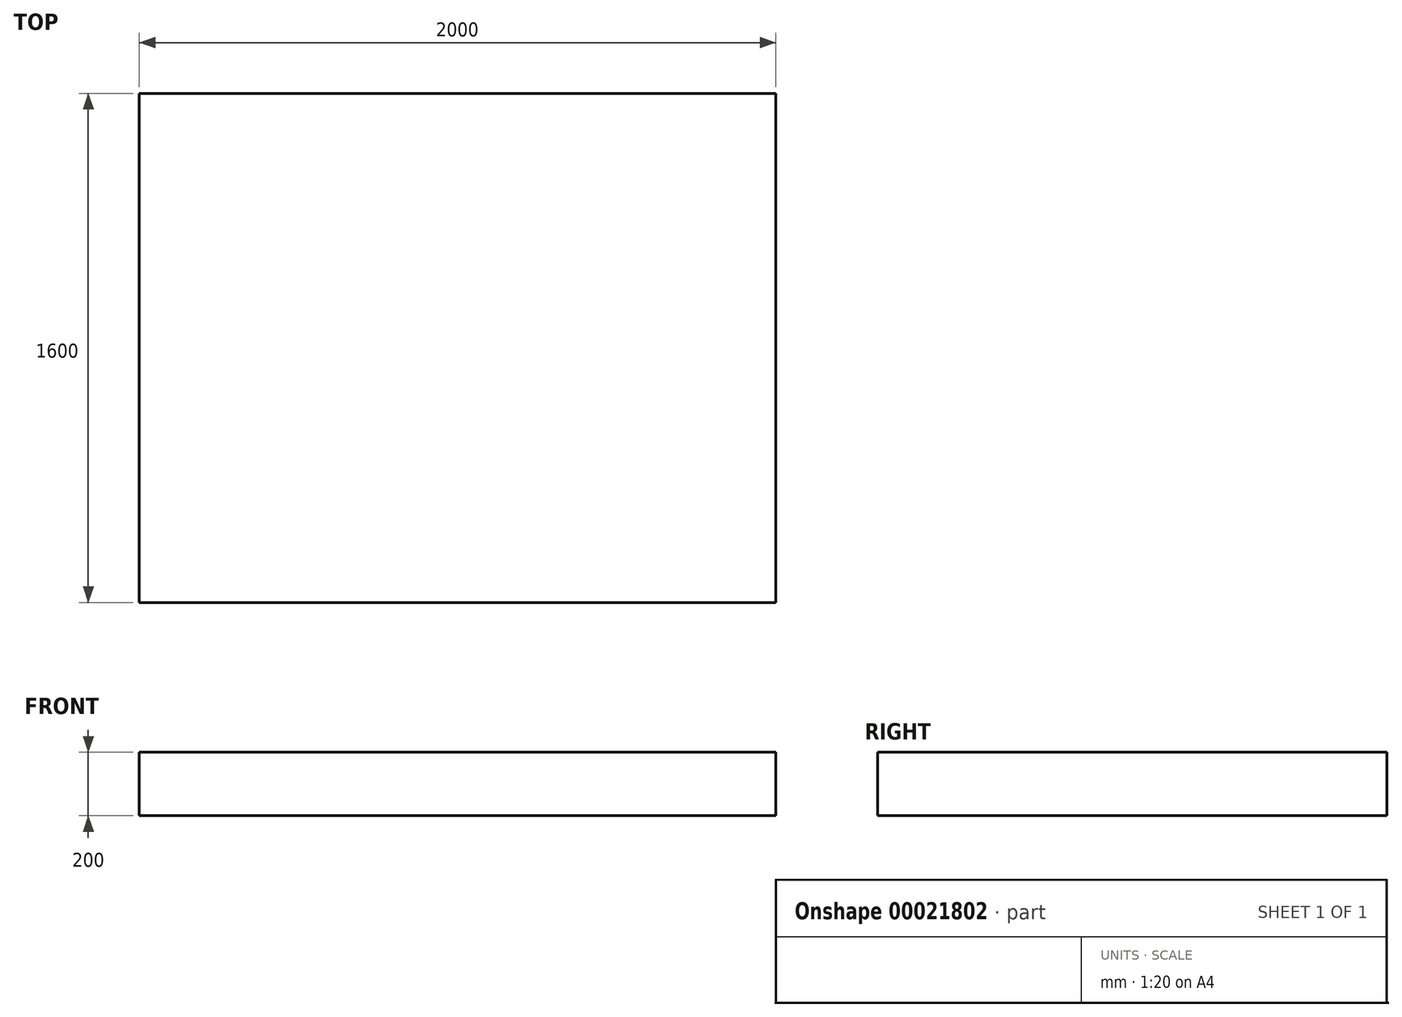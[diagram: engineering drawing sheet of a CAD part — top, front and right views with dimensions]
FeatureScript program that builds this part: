
annotation { "Feature Type Name" : "Feature", "Feature Type Description" : "" }
export const myFeature = defineFeature(function(context is Context, id is Id, definition is map)
    precondition{}
    {
        {
            var Q0;
            Q0=qCreatedBy(makeId("Top.planeOp"),FACE);
            var sketch = newSketch(context, id + "F0", { "sketchPlane" : qUnion([Q0])});
            skLineSegment(sketch, "E0.bottom", {"start": v(0, 0) * mm, "end": v(2000, 0) * mm});
            skLineSegment(sketch, "E0.top", {"start": v(0, 1600) * mm, "end": v(2000, 1600) * mm});
            skLineSegment(sketch, "E0.left", {"start": v(0, 0) * mm, "end": v(0, 1600) * mm});
            skLineSegment(sketch, "E0.right", {"start": v(2000, 0) * mm, "end": v(2000, 1600) * mm});
            skSolve(sketch);
        }
        {
            var Q0;
            Q0=makeQuery(id+"F0.imprint","IMPRINT",FACE,{"disambiguationData":[TD([[makeQuery(id+"F0.imprint","IMPRINT",EDGE,{"derivedFrom":sQuery(id+"F0.wireOp",EDGE,"E0.bottom")}),1.0]])]});
            extrude(context, id + "F1", {"entities" : qUnion([Q0]), "depth" : 200 * mm});
        }
    });
